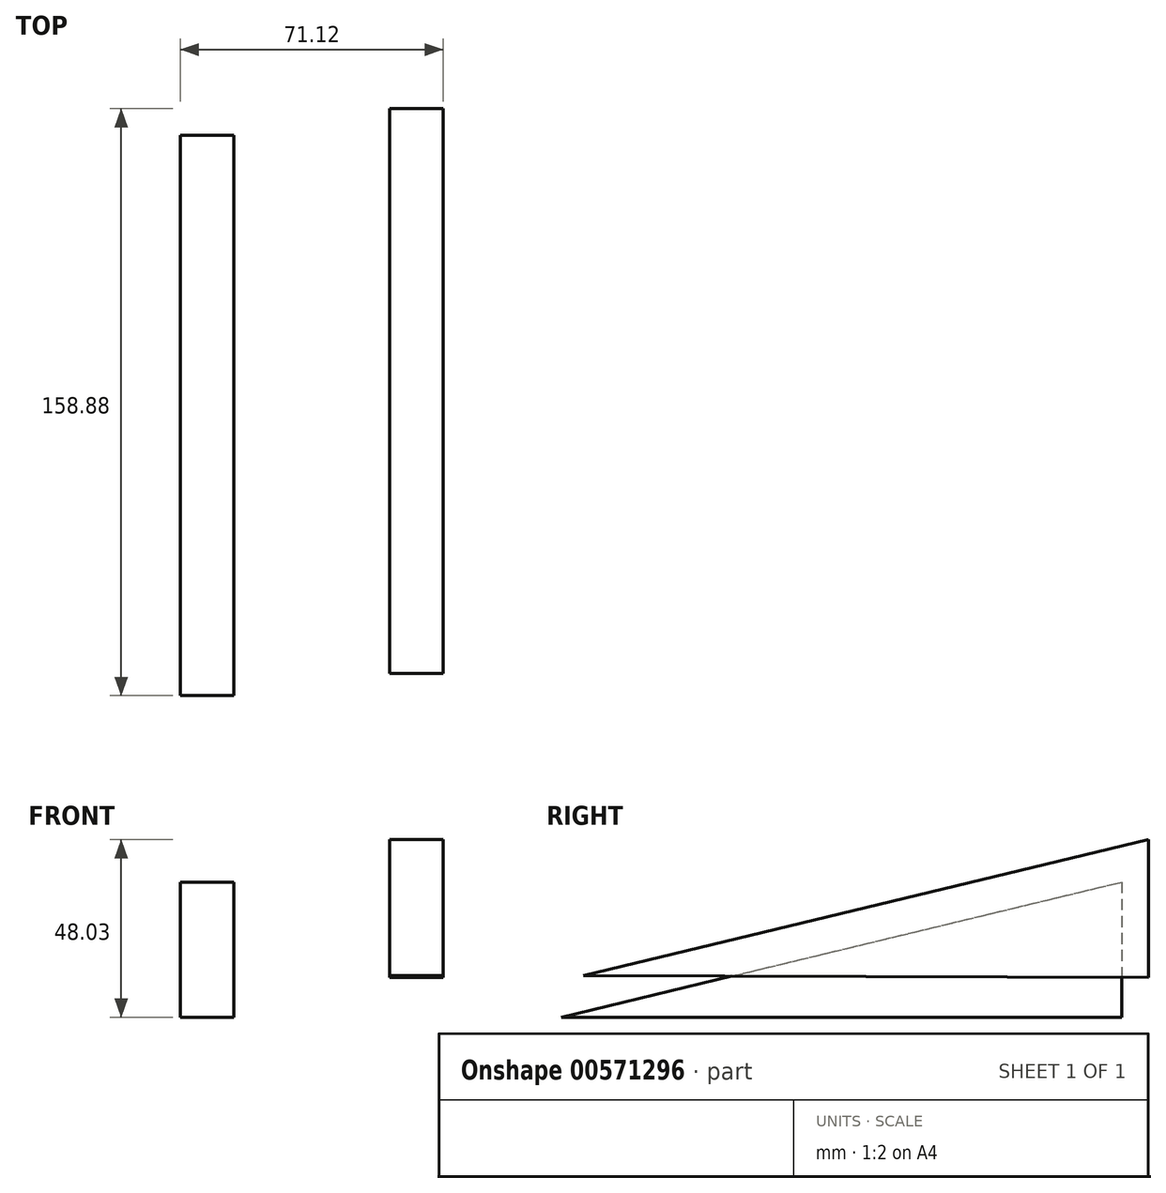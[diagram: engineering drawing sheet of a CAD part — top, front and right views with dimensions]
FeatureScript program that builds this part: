
annotation { "Feature Type Name" : "Feature", "Feature Type Description" : "" }
export const myFeature = defineFeature(function(context is Context, id is Id, definition is map)
    precondition{}
    {
        {
            var Q0;
            Q0=qCreatedBy(makeId("Right.planeOp"),FACE);
            var sketch = newSketch(context, id + "F0", { "sketchPlane" : qUnion([Q0])});
            skLineSegment(sketch, "E0", {"start": v(-76.22, 0) * mm, "end": v(75.48, 36.58) * mm});
            skLineSegment(sketch, "E1", {"start": v(75.48, 36.58) * mm, "end": v(75.48, 0) * mm});
            skLineSegment(sketch, "E2", {"start": v(75.48, 0) * mm, "end": v(-76.22, 0) * mm});
            skSolve(sketch);
        }
        {
            var Q0;
            Q0=makeQuery(id+"F0.imprint","IMPRINT",FACE,{"disambiguationData":[TD([[makeQuery(id+"F0.imprint","IMPRINT",EDGE,{"derivedFrom":sQuery(id+"F0.wireOp",EDGE,"E0")}),-1.0]])]});
            cPlane(context, id + "F1", {"entities" : qUnion([Q0]), "cplaneType" : CPlaneType.OFFSET, "offset" : 56.64 * mm, "width" : 152.4 * mm, "height" : 152.4 * mm});
        }
        {
            var Q0;
            Q0=qCreatedBy(id+"F1.planeOp",FACE);
            var sketch = newSketch(context, id + "F2", { "sketchPlane" : qUnion([Q0])});
            skLineSegment(sketch, "E3", {"start": v(-70.21, 11.24) * mm, "end": v(82.66, 48.03) * mm});
            skLineSegment(sketch, "E4", {"start": v(82.66, 48.03) * mm, "end": v(82.66, 10.71) * mm});
            skLineSegment(sketch, "E5", {"start": v(82.66, 10.71) * mm, "end": v(-70.21, 11.24) * mm});
            skSolve(sketch);
        }
        {
            var Q0;
            Q0=makeQuery(id+"F2.imprint","IMPRINT",FACE,{"disambiguationData":[TD([[makeQuery(id+"F2.imprint","IMPRINT",EDGE,{"derivedFrom":sQuery(id+"F2.wireOp",EDGE,"E3")}),-1.0]])]});
            var Q1;
            Q1=makeQuery(id+"F0.imprint","IMPRINT",FACE,{"disambiguationData":[TD([[makeQuery(id+"F0.imprint","IMPRINT",EDGE,{"derivedFrom":sQuery(id+"F0.wireOp",EDGE,"E0")}),-1.0]])]});
            extrude(context, id + "F3", {"entities" : qUnion([Q0, Q1]), "depth" : 14.48 * mm, "offsetDistance" : 25.4 * mm});
        }
    });
